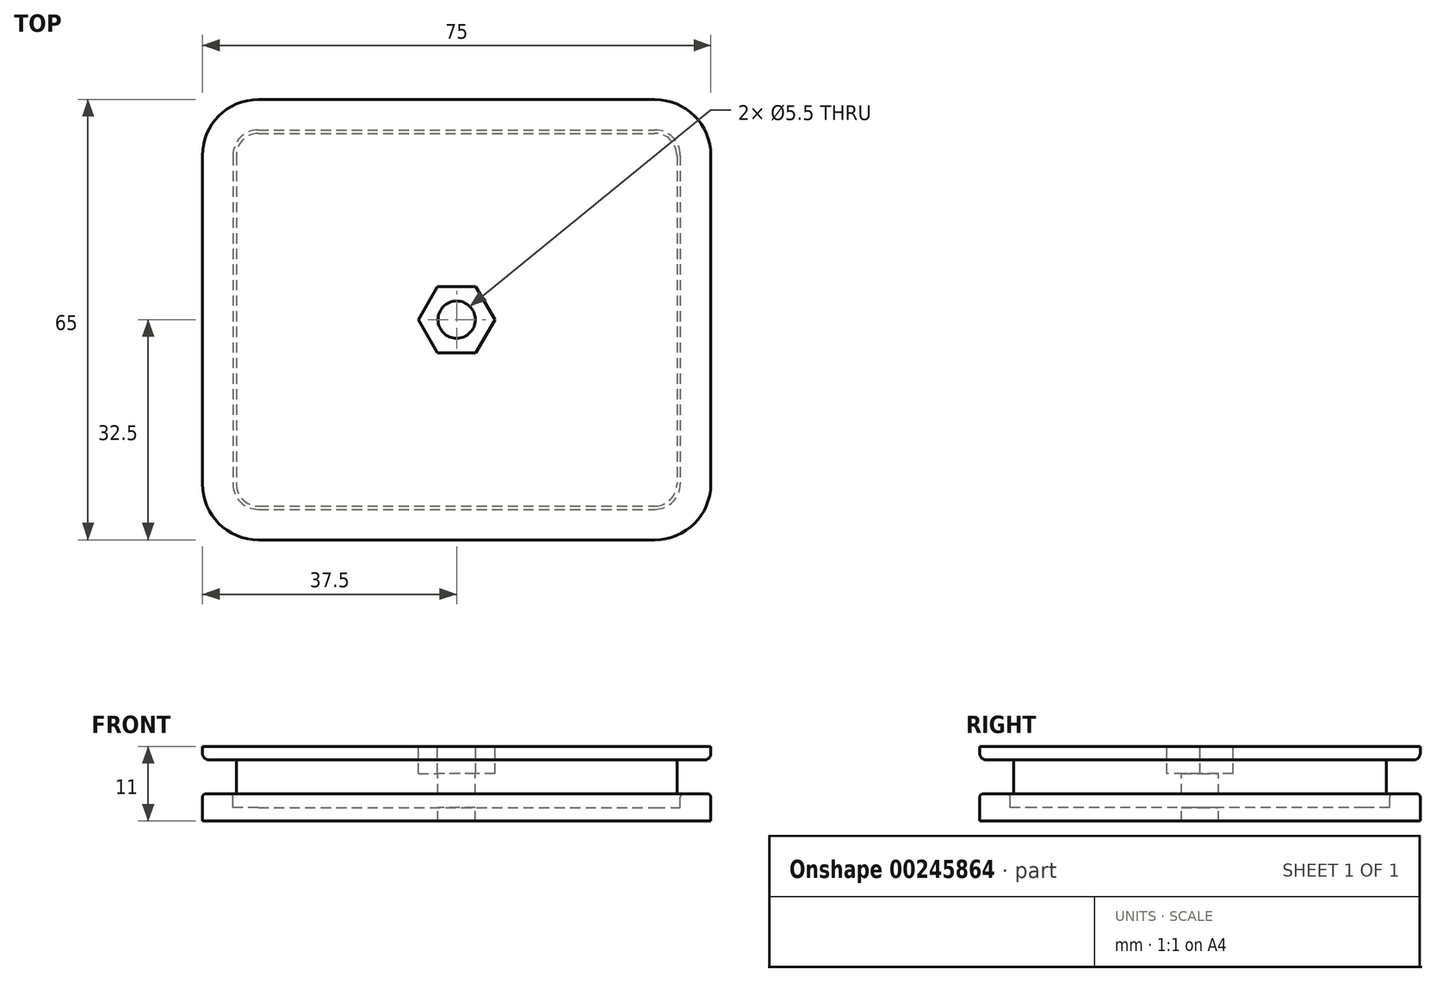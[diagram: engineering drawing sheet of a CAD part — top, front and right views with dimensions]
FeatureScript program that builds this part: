
annotation { "Feature Type Name" : "Feature", "Feature Type Description" : "" }
export const myFeature = defineFeature(function(context is Context, id is Id, definition is map)
    precondition{}
    {
        {
            var Q0;
            Q0=qCreatedBy(makeId("Top.planeOp"),FACE);
            var sketch = newSketch(context, id + "F0", { "sketchPlane" : qUnion([Q0])});
            skLineSegment(sketch, "E0.bottom", {"start": v(-29.25, 27.5) * mm, "end": v(29.25, 27.5) * mm});
            skLineSegment(sketch, "E0.top", {"start": v(-29.25, -27.5) * mm, "end": v(29.25, -27.5) * mm});
            skLineSegment(sketch, "E0.left", {"start": v(-32.5, 24.25) * mm, "end": v(-32.5, -24.25) * mm});
            skLineSegment(sketch, "E0.right", {"start": v(32.5, 24.25) * mm, "end": v(32.5, -24.25) * mm});
            skLineSegment(sketch, "E1", {"start": v(0, 27.5) * mm, "end": v(0, -27.5) * mm, "construction": true});
            skLineSegment(sketch, "E2", {"start": v(32.5, 0) * mm, "end": v(-32.5, 0) * mm, "construction": true});
            skPoint(sketch, "E3.visualSharp", {"position": v(-32.5, 27.5) * mm});
            skArc(sketch, "E3.filletArc", {"start": v(-29.25, 27.5) * mm, "mid": v(-31.55, 26.55) * mm, "end": v(-32.5, 24.25) * mm});
            skPoint(sketch, "E4.visualSharp", {"position": v(32.5, 27.5) * mm});
            skArc(sketch, "E4.filletArc", {"start": v(32.5, 24.25) * mm, "mid": v(31.55, 26.55) * mm, "end": v(29.25, 27.5) * mm});
            skPoint(sketch, "E5.visualSharp", {"position": v(32.5, -27.5) * mm});
            skArc(sketch, "E5.filletArc", {"start": v(29.25, -27.5) * mm, "mid": v(31.55, -26.55) * mm, "end": v(32.5, -24.25) * mm});
            skPoint(sketch, "E6.visualSharp", {"position": v(-32.5, -27.5) * mm});
            skArc(sketch, "E6.filletArc", {"start": v(-32.5, -24.25) * mm, "mid": v(-31.55, -26.55) * mm, "end": v(-29.25, -27.5) * mm});
            skSolve(sketch);
        }
        {
            var Q0;
            Q0=makeQuery(id+"F0.imprint","IMPRINT",FACE,{"disambiguationData":[TD([[makeQuery(id+"F0.imprint","IMPRINT",EDGE,{"derivedFrom":sQuery(id+"F0.wireOp",EDGE,"E0.bottom")}),-1.0]])]});
            extrude(context, id + "F1", {"entities" : qUnion([Q0]), "depth" : 7 * mm});
        }
        {
            var Q0;
            Q0=makeQuery(id+"F1.opExtrude","CAP_FACE",FACE,{"disambiguationData":[OSD([sQuery(id+"F0.wireOp",EDGE,"E0.bottom"),sQuery(id+"F0.wireOp",EDGE,"E0.top"),sQuery(id+"F0.wireOp",EDGE,"E0.left"),sQuery(id+"F0.wireOp",EDGE,"E0.right"),sQuery(id+"F0.wireOp",EDGE,"E3.filletArc"),sQuery(id+"F0.wireOp",EDGE,"E4.filletArc"),sQuery(id+"F0.wireOp",EDGE,"E5.filletArc"),sQuery(id+"F0.wireOp",EDGE,"E6.filletArc")])],"isStart":false});
            var sketch = newSketch(context, id + "F2", { "sketchPlane" : qUnion([Q0])});
            skArc(sketch, "E7.0", {"start": v(-29.25, 32.5) * mm, "mid": v(-35.08, 30.08) * mm, "end": v(-37.5, 24.25) * mm});
            skLineSegment(sketch, "E7.1", {"start": v(-29.25, 32.5) * mm, "end": v(29.25, 32.5) * mm});
            skLineSegment(sketch, "E7.2", {"start": v(-37.5, 24.25) * mm, "end": v(-37.5, -24.25) * mm});
            skArc(sketch, "E7.3", {"start": v(37.5, 24.25) * mm, "mid": v(35.08, 30.08) * mm, "end": v(29.25, 32.5) * mm});
            skArc(sketch, "E7.4", {"start": v(-37.5, -24.25) * mm, "mid": v(-35.08, -30.08) * mm, "end": v(-29.25, -32.5) * mm});
            skLineSegment(sketch, "E7.5", {"start": v(-29.25, -32.5) * mm, "end": v(29.25, -32.5) * mm});
            skArc(sketch, "E7.6", {"start": v(29.25, -32.5) * mm, "mid": v(35.08, -30.08) * mm, "end": v(37.5, -24.25) * mm});
            skLineSegment(sketch, "E7.7", {"start": v(37.5, 24.25) * mm, "end": v(37.5, -24.25) * mm});
            skSolve(sketch);
        }
        {
            var Q0;
            Q0 = qSketchRegion(id + "F2", true);
            extrude(context, id + "F3", {"entities" : qUnion([Q0]), "operationType" : NewBodyOperationType.ADD, "depth" : 2 * mm});
        }
        {
            var Q0;
            Q0 = qSketchRegion(id + "F2", true);
            extrude(context, id + "F4", {"entities" : qUnion([Q0]), "depth" : 4 * mm});
        }
        {
            var Q0;
            Q0=makeQuery(id+"F4.opExtrude","SWEPT_BODY",BODY,{"disambiguationData":[OSD([sQuery(id+"F2.wireOp",EDGE,"E7.0"),sQuery(id+"F2.wireOp",EDGE,"E7.1"),sQuery(id+"F2.wireOp",EDGE,"E7.2"),sQuery(id+"F2.wireOp",EDGE,"E7.3"),sQuery(id+"F2.wireOp",EDGE,"E7.4"),sQuery(id+"F2.wireOp",EDGE,"E7.5"),sQuery(id+"F2.wireOp",EDGE,"E7.6"),sQuery(id+"F2.wireOp",EDGE,"E7.7")])]});
            transform(context, id + "F5", {"entities" : qUnion([Q0]), "transformType" : TransformType.TRANSLATION_3D, "dx" : 0 * mm, "dy" : 0 * mm, "dz" : -9 * mm, "makeCopy" : false});
        }
        {
            var Q0;
            Q0=makeQuery(id+"F4.opExtrude","CAP_FACE",FACE,{"disambiguationData":[OSD([sQuery(id+"F2.wireOp",EDGE,"E7.0"),sQuery(id+"F2.wireOp",EDGE,"E7.1"),sQuery(id+"F2.wireOp",EDGE,"E7.2"),sQuery(id+"F2.wireOp",EDGE,"E7.3"),sQuery(id+"F2.wireOp",EDGE,"E7.4"),sQuery(id+"F2.wireOp",EDGE,"E7.5"),sQuery(id+"F2.wireOp",EDGE,"E7.6"),sQuery(id+"F2.wireOp",EDGE,"E7.7")])],"isStart":false});
            var sketch = newSketch(context, id + "F6", { "sketchPlane" : qUnion([Q0])});
            skArc(sketch, "E8.0", {"start": v(-29.25, 28) * mm, "mid": v(-31.9, 26.9) * mm, "end": v(-33, 24.25) * mm});
            skLineSegment(sketch, "E8.1", {"start": v(-33, 24.25) * mm, "end": v(-33, -24.25) * mm});
            skLineSegment(sketch, "E8.2", {"start": v(-29.25, 28) * mm, "end": v(29.25, 28) * mm});
            skArc(sketch, "E8.3", {"start": v(-33, -24.25) * mm, "mid": v(-31.9, -26.9) * mm, "end": v(-29.25, -28) * mm});
            skArc(sketch, "E8.4", {"start": v(33, 24.25) * mm, "mid": v(31.9, 26.9) * mm, "end": v(29.25, 28) * mm});
            skLineSegment(sketch, "E8.5", {"start": v(33, 24.25) * mm, "end": v(33, -24.25) * mm});
            skArc(sketch, "E8.6", {"start": v(29.25, -28) * mm, "mid": v(31.9, -26.9) * mm, "end": v(33, -24.25) * mm});
            skLineSegment(sketch, "E8.7", {"start": v(-29.25, -28) * mm, "end": v(29.25, -28) * mm});
            skSolve(sketch);
        }
        {
            var Q0;
            Q0=makeQuery(id+"F6.imprint","IMPRINT",FACE,{"disambiguationData":[TD([[makeQuery(id+"F6.imprint","IMPRINT",EDGE,{"derivedFrom":sQuery(id+"F6.wireOp",EDGE,"E8.0")}),1.0]])]});
            extrude(context, id + "F7", {"entities" : qUnion([Q0]), "operationType" : NewBodyOperationType.REMOVE, "oppositeDirection" : true, "depth" : 2 * mm});
        }
        {
            var Q0;
            Q0=makeQuery(id+"F4.opExtrude","CAP_FACE",FACE,{"disambiguationData":[OSD([sQuery(id+"F2.wireOp",EDGE,"E7.0"),sQuery(id+"F2.wireOp",EDGE,"E7.1"),sQuery(id+"F2.wireOp",EDGE,"E7.2"),sQuery(id+"F2.wireOp",EDGE,"E7.3"),sQuery(id+"F2.wireOp",EDGE,"E7.4"),sQuery(id+"F2.wireOp",EDGE,"E7.5"),sQuery(id+"F2.wireOp",EDGE,"E7.6"),sQuery(id+"F2.wireOp",EDGE,"E7.7")])],"isStart":false});
            fillet(context, id + "F8", {"entities" : qUnion([Q0]), "radius" : 0.5 * mm, "tangentPropagation" : true, "allowEdgeOverflow" : false});
        }
        {
            var Q0;
            Q0=makeQuery(id+"F3.opExtrude","CAP_FACE",FACE,{"disambiguationData":[OSD([sQuery(id+"F2.wireOp",EDGE,"E7.0"),sQuery(id+"F2.wireOp",EDGE,"E7.1"),sQuery(id+"F2.wireOp",EDGE,"E7.2"),sQuery(id+"F2.wireOp",EDGE,"E7.3"),sQuery(id+"F2.wireOp",EDGE,"E7.4"),sQuery(id+"F2.wireOp",EDGE,"E7.5"),sQuery(id+"F2.wireOp",EDGE,"E7.6"),sQuery(id+"F2.wireOp",EDGE,"E7.7")])],"isStart":false});
            var sketch = newSketch(context, id + "F9", { "sketchPlane" : qUnion([Q0])});
            skPoint(sketch, "E9", {"position": v(0, 0) * mm});
            skCircle(sketch, "E10.cCircle", {"center": v(0, 0) * mm, "radius": 4.9 * mm, "construction": true});
            skLineSegment(sketch, "E10.0", {"start": v(2.83, -4.9) * mm, "end": v(-2.83, -4.9) * mm});
            skLineSegment(sketch, "E10.1", {"start": v(-2.83, -4.9) * mm, "end": v(-5.66, 0) * mm});
            skLineSegment(sketch, "E10.2", {"start": v(-5.66, 0) * mm, "end": v(-2.83, 4.9) * mm});
            skLineSegment(sketch, "E10.3", {"start": v(-2.83, 4.9) * mm, "end": v(2.83, 4.9) * mm});
            skLineSegment(sketch, "E10.4", {"start": v(2.83, 4.9) * mm, "end": v(5.66, 0) * mm});
            skLineSegment(sketch, "E10.5", {"start": v(5.66, 0) * mm, "end": v(2.83, -4.9) * mm});
            skPoint(sketch, "E10.0.midPoint", {"position": v(0, -4.9) * mm});
            skSolve(sketch);
        }
        {
            var Q0;
            Q0=sQuery(id+"F9.wireOp",VERTEX,"E9");
            var Q1;
            Q1=makeQuery(id+"F1.opExtrude","SWEPT_BODY",BODY,{"disambiguationData":[OSD([sQuery(id+"F0.wireOp",EDGE,"E0.bottom"),sQuery(id+"F0.wireOp",EDGE,"E0.top"),sQuery(id+"F0.wireOp",EDGE,"E0.left"),sQuery(id+"F0.wireOp",EDGE,"E0.right"),sQuery(id+"F0.wireOp",EDGE,"E3.filletArc"),sQuery(id+"F0.wireOp",EDGE,"E4.filletArc"),sQuery(id+"F0.wireOp",EDGE,"E5.filletArc"),sQuery(id+"F0.wireOp",EDGE,"E6.filletArc")])]});
            var Q2;
            Q2=makeQuery(id+"F4.opExtrude","SWEPT_BODY",BODY,{"disambiguationData":[OSD([sQuery(id+"F2.wireOp",EDGE,"E7.0"),sQuery(id+"F2.wireOp",EDGE,"E7.1"),sQuery(id+"F2.wireOp",EDGE,"E7.2"),sQuery(id+"F2.wireOp",EDGE,"E7.3"),sQuery(id+"F2.wireOp",EDGE,"E7.4"),sQuery(id+"F2.wireOp",EDGE,"E7.5"),sQuery(id+"F2.wireOp",EDGE,"E7.6"),sQuery(id+"F2.wireOp",EDGE,"E7.7")])]});
            hole(context, id + "F10", {"style" : HoleStyle.C_BORE, "endStyle" : HoleEndStyle.THROUGH, "holeDiameter" : 5.5 * mm, "cBoreDiameter" : 6.5 * mm, "cBoreDepth" : 3 * mm, "tappedDepth" : 12 * mm, "tapClearance" : 3, "locations" : qUnion([Q0]), "scope" : qUnion([Q1, Q2])});
        }
        {
            var Q0;
            Q0 = qSketchRegion(id + "F9", true);
            extrude(context, id + "F11", {"entities" : qUnion([Q0]), "operationType" : NewBodyOperationType.REMOVE, "oppositeDirection" : true, "depth" : 4 * mm});
        }
        {
            var Q0;
            Q0=makeQuery(id+"F3.opExtrude","CAP_EDGE",EDGE,{"disambiguationData":[OSD([sQuery(id+"F2.wireOp",EDGE,"E7.7")])],"isStart":true});
            var Q1;
            Q1=makeQuery(id+"F3.opExtrude","CAP_EDGE",EDGE,{"disambiguationData":[OSD([sQuery(id+"F2.wireOp",EDGE,"E7.6")])],"isStart":true});
            var Q2;
            Q2=makeQuery(id+"F3.opExtrude","CAP_EDGE",EDGE,{"disambiguationData":[OSD([sQuery(id+"F2.wireOp",EDGE,"E7.5")])],"isStart":true});
            var Q3;
            Q3=makeQuery(id+"F3.opExtrude","CAP_EDGE",EDGE,{"disambiguationData":[OSD([sQuery(id+"F2.wireOp",EDGE,"E7.4")])],"isStart":true});
            var Q4;
            Q4=makeQuery(id+"F3.opExtrude","CAP_EDGE",EDGE,{"disambiguationData":[OSD([sQuery(id+"F2.wireOp",EDGE,"E7.2")])],"isStart":true});
            var Q5;
            Q5=makeQuery(id+"F3.opExtrude","CAP_EDGE",EDGE,{"disambiguationData":[OSD([sQuery(id+"F2.wireOp",EDGE,"E7.0")])],"isStart":true});
            var Q6;
            Q6=makeQuery(id+"F3.opExtrude","CAP_EDGE",EDGE,{"disambiguationData":[OSD([sQuery(id+"F2.wireOp",EDGE,"E7.1")])],"isStart":true});
            var Q7;
            Q7=makeQuery(id+"F3.opExtrude","CAP_EDGE",EDGE,{"disambiguationData":[OSD([sQuery(id+"F2.wireOp",EDGE,"E7.3")])],"isStart":true});
            fillet(context, id + "F12", {"entities" : qUnion([Q0, Q1, Q2, Q3, Q4, Q5, Q6, Q7]), "radius" : 1 * mm, "tangentPropagation" : true, "allowEdgeOverflow" : false});
        }
    });
